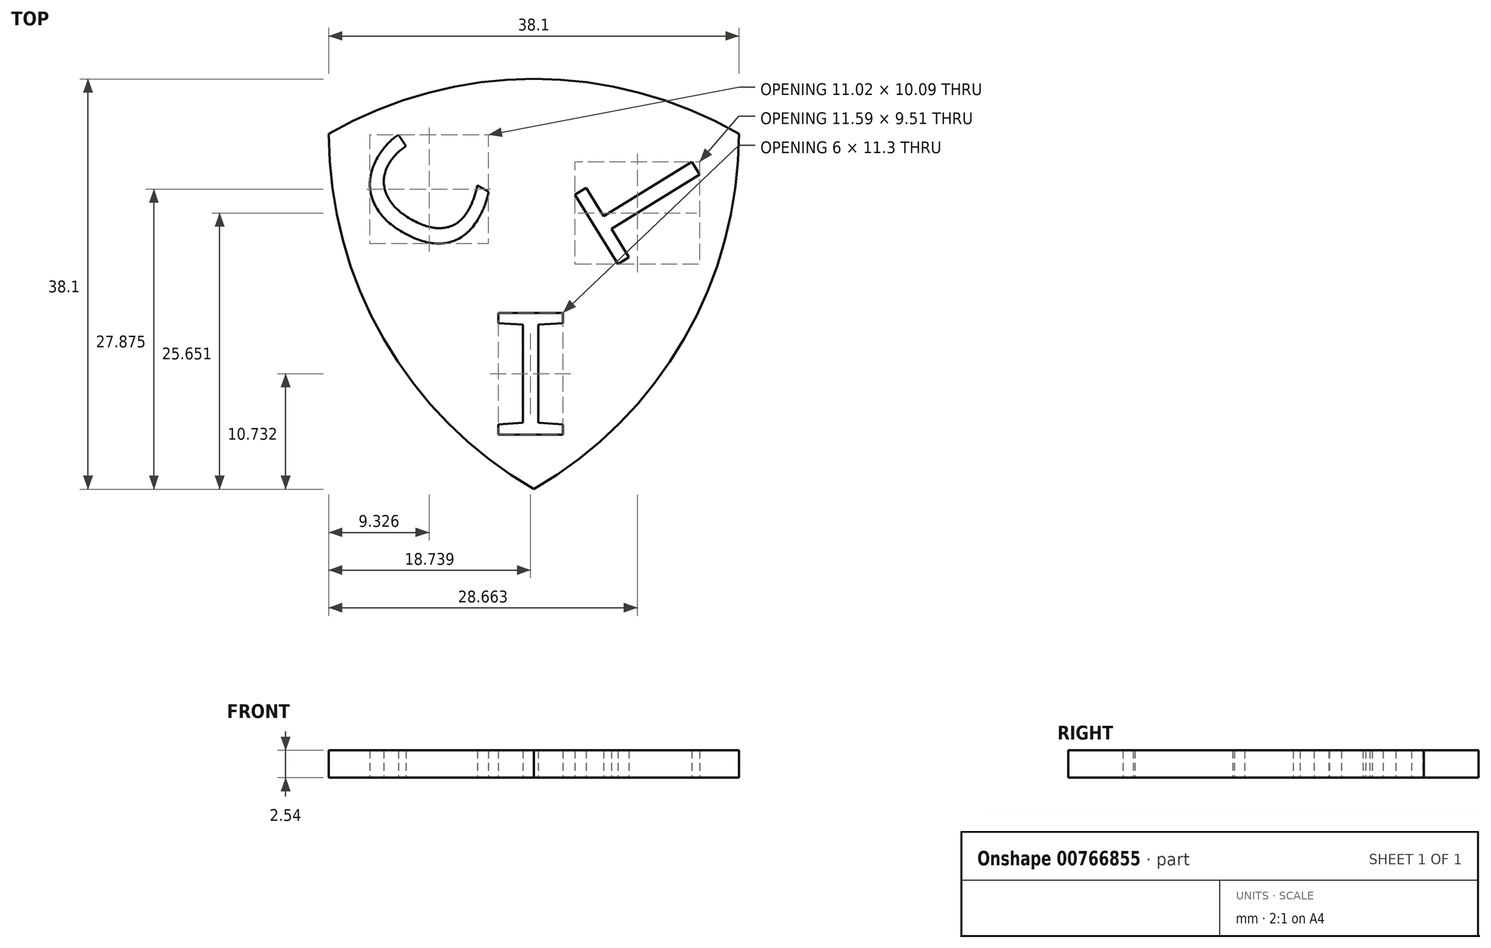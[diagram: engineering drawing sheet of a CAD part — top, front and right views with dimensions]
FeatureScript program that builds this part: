
annotation { "Feature Type Name" : "Feature", "Feature Type Description" : "" }
export const myFeature = defineFeature(function(context is Context, id is Id, definition is map)
    precondition{}
    {
        {
            var Q0;
            Q0=qCreatedBy(makeId("Top.planeOp"),FACE);
            var sketch = newSketch(context, id + "F0", { "sketchPlane" : qUnion([Q0])});
            skCircle(sketch, "E0", {"center": v(0, 0) * mm, "radius": 38.1 * mm});
            skSolve(sketch);
        }
        {
            var Q0;
            Q0=qCreatedBy(makeId("Top.planeOp"),FACE);
            var sketch = newSketch(context, id + "F1", { "sketchPlane" : qUnion([Q0])});
            skCircle(sketch, "E1", {"center": v(-38.1, 0) * mm, "radius": 38.1 * mm});
            skSolve(sketch);
        }
        {
            var Q0;
            Q0=qCreatedBy(makeId("Top.planeOp"),FACE);
            var sketch = newSketch(context, id + "F2", { "sketchPlane" : qUnion([Q0])});
            skCircle(sketch, "E2", {"center": v(-19.05, -33) * mm, "radius": 38.1 * mm});
            skSolve(sketch);
        }
        {
            var Q0;
            Q0 = qSketchRegion(id + "F0", true);
            extrude(context, id + "F3", {"entities" : qUnion([Q0]), "depth" : 2.54 * mm, "offsetDistance" : 25.4 * mm});
        }
        {
            var Q0;
            Q0 = qSketchRegion(id + "F1", true);
            extrude(context, id + "F4", {"entities" : qUnion([Q0]), "depth" : 2.54 * mm, "offsetDistance" : 25.4 * mm});
        }
        {
            var Q0;
            Q0 = qSketchRegion(id + "F2", true);
            extrude(context, id + "F5", {"entities" : qUnion([Q0]), "depth" : 2.54 * mm, "offsetDistance" : 25.4 * mm});
        }
        {
            var Q0;
            Q0=makeQuery(id+"F3.opExtrude","SWEPT_BODY",BODY,{"disambiguationData":[OSD([sQuery(id+"F0.wireOp",EDGE,"E0")])]});
            var Q1;
            Q1=makeQuery(id+"F4.opExtrude","SWEPT_BODY",BODY,{"disambiguationData":[OSD([sQuery(id+"F1.wireOp",EDGE,"E1")])]});
            var Q2;
            Q2=makeQuery(id+"F5.opExtrude","SWEPT_BODY",BODY,{"disambiguationData":[OSD([sQuery(id+"F2.wireOp",EDGE,"E2")])]});
            booleanBodies(context, id + "F6", {"operationType" : BooleanOperationType.INTERSECTION, "tools" : qUnion([Q0, Q1, Q2])});
        }
        {
            var Q0;
            Q0=qCreatedBy(makeId("Top.planeOp"),FACE);
            var sketch = newSketch(context, id + "F7", { "sketchPlane" : qUnion([Q0])});
            skText(sketch, "E3", { "text": "C", "fontName": "DroidSansMono.ttf"});
            skText(sketch, "E4", { "text": "T", "fontName": "DroidSansMono.ttf"});
            skText(sketch, "E5", { "text": "I", "fontName": "DroidSansMono.ttf"});
            const initialGuessF7  = {"E3": [-0.02711, -0.0126, 0.5, 0.86603, 0.01073], "E4": [-0.00162, -0.00706, -0.52446, 0.85144, 0.01094], "E5": [-0.0241, -0.02792, 1, 0, 0.0114]};
            skSetInitialGuess(sketch, initialGuessF7);
            skSolve(sketch);
        }
        {
            var Q0;
            Q0 = qSketchRegion(id + "F7", true);
            extrude(context, id + "F8", {"entities" : qUnion([Q0]), "depth" : 2.54 * mm, "offsetDistance" : 25.4 * mm});
        }
        {
            var Q0;
            Q0=makeQuery(id+"F8.opExtrude","SWEPT_BODY",BODY,{"disambiguationData":[OSD([sQuery(id+"F7.wireOp",EDGE,"E3.sketch_text.stroke-0"),sQuery(id+"F7.wireOp",EDGE,"E3.sketch_text.stroke-1"),sQuery(id+"F7.wireOp",EDGE,"E3.sketch_text.stroke-2"),sQuery(id+"F7.wireOp",EDGE,"E3.sketch_text.stroke-3"),sQuery(id+"F7.wireOp",EDGE,"E3.sketch_text.stroke-4"),sQuery(id+"F7.wireOp",EDGE,"E3.sketch_text.stroke-5"),sQuery(id+"F7.wireOp",EDGE,"E3.sketch_text.stroke-6"),sQuery(id+"F7.wireOp",EDGE,"E3.sketch_text.stroke-7"),sQuery(id+"F7.wireOp",EDGE,"E3.sketch_text.stroke-8"),sQuery(id+"F7.wireOp",EDGE,"E3.sketch_text.stroke-9"),sQuery(id+"F7.wireOp",EDGE,"E3.sketch_text.stroke-10"),sQuery(id+"F7.wireOp",EDGE,"E3.sketch_text.stroke-11"),sQuery(id+"F7.wireOp",EDGE,"E3.sketch_text.stroke-12"),sQuery(id+"F7.wireOp",EDGE,"E3.sketch_text.stroke-13")])]});
            var Q1;
            Q1=makeQuery(id+"F8.opExtrude","SWEPT_BODY",BODY,{"disambiguationData":[OSD([sQuery(id+"F7.wireOp",EDGE,"E4.sketch_text.stroke-0"),sQuery(id+"F7.wireOp",EDGE,"E4.sketch_text.stroke-1"),sQuery(id+"F7.wireOp",EDGE,"E4.sketch_text.stroke-2"),sQuery(id+"F7.wireOp",EDGE,"E4.sketch_text.stroke-3"),sQuery(id+"F7.wireOp",EDGE,"E4.sketch_text.stroke-4"),sQuery(id+"F7.wireOp",EDGE,"E4.sketch_text.stroke-5"),sQuery(id+"F7.wireOp",EDGE,"E4.sketch_text.stroke-6"),sQuery(id+"F7.wireOp",EDGE,"E4.sketch_text.stroke-7")])]});
            var Q2;
            Q2=makeQuery(id+"F8.opExtrude","SWEPT_BODY",BODY,{"disambiguationData":[OSD([sQuery(id+"F7.wireOp",EDGE,"E5.sketch_text.stroke-0"),sQuery(id+"F7.wireOp",EDGE,"E5.sketch_text.stroke-1"),sQuery(id+"F7.wireOp",EDGE,"E5.sketch_text.stroke-2"),sQuery(id+"F7.wireOp",EDGE,"E5.sketch_text.stroke-3"),sQuery(id+"F7.wireOp",EDGE,"E5.sketch_text.stroke-4"),sQuery(id+"F7.wireOp",EDGE,"E5.sketch_text.stroke-5"),sQuery(id+"F7.wireOp",EDGE,"E5.sketch_text.stroke-6"),sQuery(id+"F7.wireOp",EDGE,"E5.sketch_text.stroke-7"),sQuery(id+"F7.wireOp",EDGE,"E5.sketch_text.stroke-8"),sQuery(id+"F7.wireOp",EDGE,"E5.sketch_text.stroke-9"),sQuery(id+"F7.wireOp",EDGE,"E5.sketch_text.stroke-10"),sQuery(id+"F7.wireOp",EDGE,"E5.sketch_text.stroke-11")])]});
            var Q3;
            Q3=makeQuery(id+"F6.opBoolean","INTERSECT",BODY,{"derivedFrom":[makeQuery(id+"F3.opExtrude","SWEPT_BODY",BODY,{"disambiguationData":[OSD([sQuery(id+"F0.wireOp",EDGE,"E0")])]}),makeQuery(id+"F4.opExtrude","SWEPT_BODY",BODY,{"disambiguationData":[OSD([sQuery(id+"F1.wireOp",EDGE,"E1")])]}),makeQuery(id+"F5.opExtrude","SWEPT_BODY",BODY,{"disambiguationData":[OSD([sQuery(id+"F2.wireOp",EDGE,"E2")])]})]});
            booleanBodies(context, id + "F9", {"operationType" : BooleanOperationType.SUBTRACTION, "tools" : qUnion([Q0, Q1, Q2]), "targets" : qUnion([Q3])});
        }
    });
